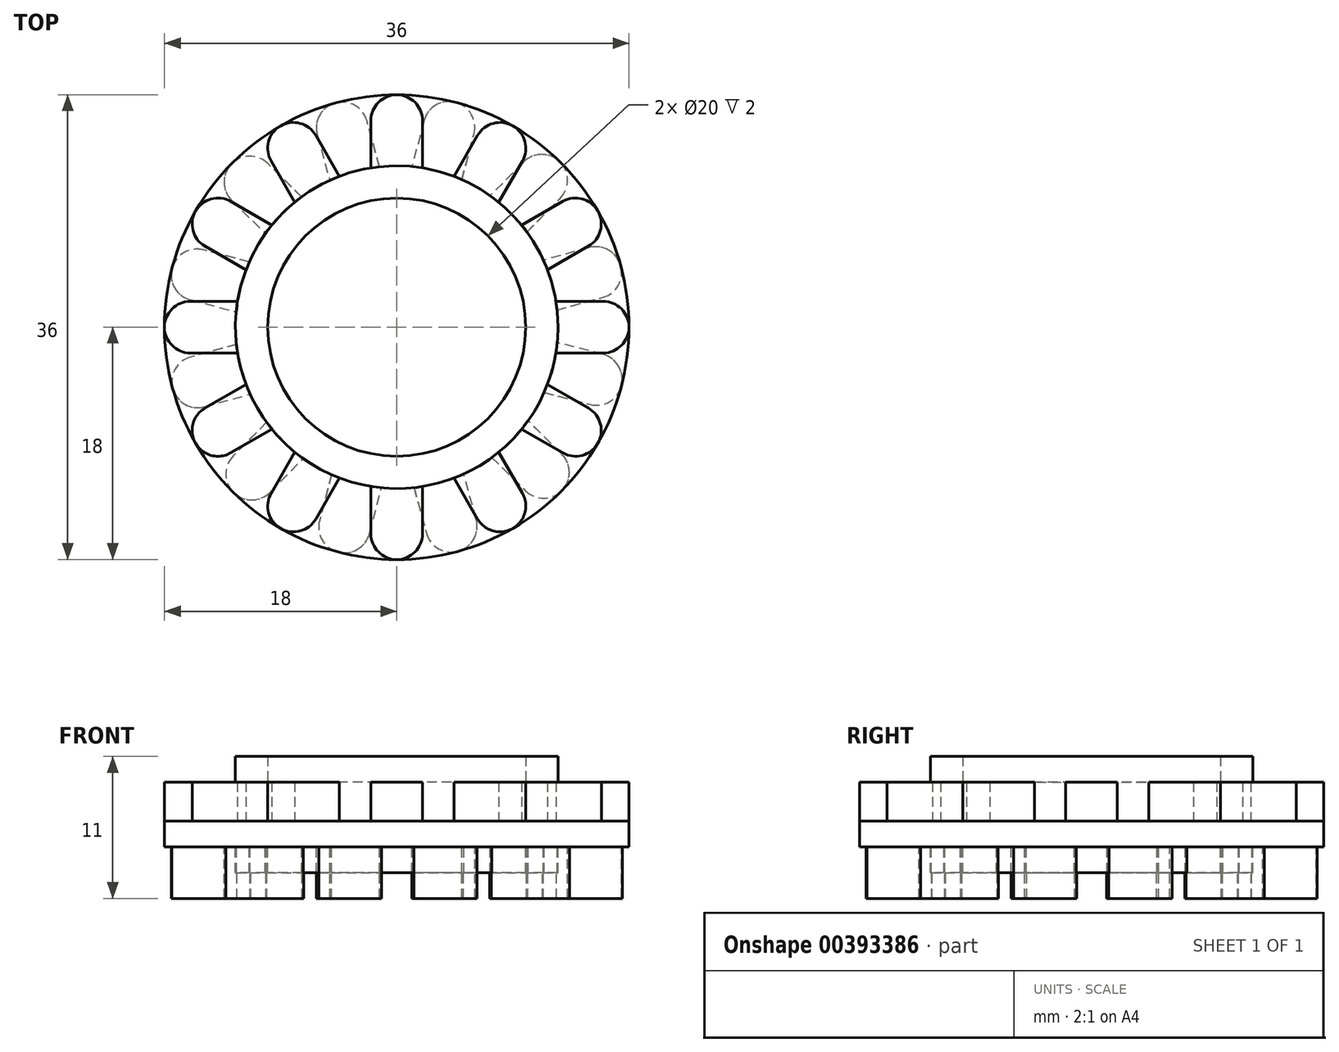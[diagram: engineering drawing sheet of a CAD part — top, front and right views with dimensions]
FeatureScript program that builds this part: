
annotation { "Feature Type Name" : "Feature", "Feature Type Description" : "" }
export const myFeature = defineFeature(function(context is Context, id is Id, definition is map)
    precondition{}
    {
        {
            var Q0;
            Q0=qCreatedBy(makeId("Top.planeOp"),FACE);
            var sketch = newSketch(context, id + "F0", { "sketchPlane" : qUnion([Q0])});
            skCircle(sketch, "E0", {"center": v(0, 0) * mm, "radius": 18 * mm});
            skSolve(sketch);
        }
        {
            var Q0;
            Q0=makeQuery(id+"F0.imprint","IMPRINT",FACE,{"disambiguationData":[TD([[makeQuery(id+"F0.imprint","IMPRINT",EDGE,{"derivedFrom":sQuery(id+"F0.wireOp",EDGE,"E0")}),1.0]])]});
            extrude(context, id + "F1", {"entities" : qUnion([Q0]), "depth" : 2 * mm});
        }
        {
            var Q0;
            Q0=makeQuery(id+"F1.opExtrude","CAP_FACE",FACE,{"disambiguationData":[OSD([sQuery(id+"F0.wireOp",EDGE,"E0")])],"isStart":false});
            var sketch = newSketch(context, id + "F2", { "sketchPlane" : qUnion([Q0])});
            skCircle(sketch, "E1", {"center": v(0, 0) * mm, "radius": 10 * mm});
            skCircle(sketch, "E2", {"center": v(0, 0) * mm, "radius": 12.5 * mm});
            skSolve(sketch);
        }
        {
            var Q0;
            Q0=makeQuery(id+"F2.imprint","IMPRINT",FACE,{"disambiguationData":[TD([[makeQuery(id+"F2.imprint","IMPRINT",EDGE,{"derivedFrom":sQuery(id+"F2.wireOp",EDGE,"E1")}),-1.0]])]});
            extrude(context, id + "F3", {"entities" : qUnion([Q0]), "operationType" : NewBodyOperationType.ADD, "depth" : 5 * mm});
        }
        {
            var Q0;
            Q0 = qSketchRegion(id + "F2", true);
            extrude(context, id + "F4", {"entities" : qUnion([Q0]), "operationType" : NewBodyOperationType.ADD, "oppositeDirection" : true, "depth" : 4 * mm});
        }
        {
            var Q0;
            {var subQ0=sQuery(id+"F0.wireOp",EDGE,"E0");Q0=makeQuery(id+"F3.boolean.opBoolean","SPLIT",FACE,{"disambiguationData":[TD([makeQuery(id+"F1.opExtrude","SWEPT_FACE",FACE,{"disambiguationData":[OSD([subQ0])]})])],"derivedFrom":makeQuery(id+"F1.opExtrude","CAP_FACE",FACE,{"disambiguationData":[OSD([subQ0])],"isStart":false})});}
            var sketch = newSketch(context, id + "F5", { "sketchPlane" : qUnion([Q0])});
            skLineSegment(sketch, "E3.3.0", {"start": v(2, 12.34) * mm, "end": v(2, 16) * mm});
            skLineSegment(sketch, "E3.3.1", {"start": v(-2, 12.34) * mm, "end": v(-2, 16) * mm});
            skPoint(sketch, "E3.center", {"position": v(0, 0) * mm});
            skArc(sketch, "E4", {"start": v(2, 16) * mm, "mid": v(0, 18) * mm, "end": v(-2, 16) * mm});
            skLineSegment(sketch, "E5.1.0", {"start": v(-4.44, 11.69) * mm, "end": v(-6.27, 14.86) * mm});
            skLineSegment(sketch, "E5.1.1", {"start": v(-7.9, 9.69) * mm, "end": v(-9.73, 12.86) * mm});
            skArc(sketch, "E5.1.2", {"start": v(-6.27, 14.86) * mm, "mid": v(-9, 15.59) * mm, "end": v(-9.73, 12.86) * mm});
            skLineSegment(sketch, "E5.2.0", {"start": v(-9.69, 7.9) * mm, "end": v(-12.86, 9.73) * mm});
            skLineSegment(sketch, "E5.2.1", {"start": v(-11.69, 4.44) * mm, "end": v(-14.86, 6.27) * mm});
            skArc(sketch, "E5.2.2", {"start": v(-12.86, 9.73) * mm, "mid": v(-15.59, 9) * mm, "end": v(-14.86, 6.27) * mm});
            skLineSegment(sketch, "E5.3.0", {"start": v(-12.34, 2) * mm, "end": v(-16, 2) * mm});
            skLineSegment(sketch, "E5.3.1", {"start": v(-12.34, -2) * mm, "end": v(-16, -2) * mm});
            skArc(sketch, "E5.3.2", {"start": v(-16, 2) * mm, "mid": v(-18, 0) * mm, "end": v(-16, -2) * mm});
            skLineSegment(sketch, "E5.4.0", {"start": v(-11.69, -4.44) * mm, "end": v(-14.86, -6.27) * mm});
            skLineSegment(sketch, "E5.4.1", {"start": v(-9.69, -7.9) * mm, "end": v(-12.86, -9.73) * mm});
            skArc(sketch, "E5.4.2", {"start": v(-14.86, -6.27) * mm, "mid": v(-15.59, -9) * mm, "end": v(-12.86, -9.73) * mm});
            skLineSegment(sketch, "E5.5.0", {"start": v(-7.9, -9.69) * mm, "end": v(-9.73, -12.86) * mm});
            skLineSegment(sketch, "E5.5.1", {"start": v(-4.44, -11.69) * mm, "end": v(-6.27, -14.86) * mm});
            skArc(sketch, "E5.5.2", {"start": v(-9.73, -12.86) * mm, "mid": v(-9, -15.59) * mm, "end": v(-6.27, -14.86) * mm});
            skLineSegment(sketch, "E5.6.0", {"start": v(-2, -12.34) * mm, "end": v(-2, -16) * mm});
            skLineSegment(sketch, "E5.6.1", {"start": v(2, -12.34) * mm, "end": v(2, -16) * mm});
            skArc(sketch, "E5.6.2", {"start": v(-2, -16) * mm, "mid": v(0, -18) * mm, "end": v(2, -16) * mm});
            skLineSegment(sketch, "E5.7.0", {"start": v(4.44, -11.69) * mm, "end": v(6.27, -14.86) * mm});
            skLineSegment(sketch, "E5.7.1", {"start": v(7.9, -9.69) * mm, "end": v(9.73, -12.86) * mm});
            skArc(sketch, "E5.7.2", {"start": v(6.27, -14.86) * mm, "mid": v(9, -15.59) * mm, "end": v(9.73, -12.86) * mm});
            skLineSegment(sketch, "E5.8.0", {"start": v(9.69, -7.9) * mm, "end": v(12.86, -9.73) * mm});
            skLineSegment(sketch, "E5.8.1", {"start": v(11.69, -4.44) * mm, "end": v(14.86, -6.27) * mm});
            skArc(sketch, "E5.8.2", {"start": v(12.86, -9.73) * mm, "mid": v(15.59, -9) * mm, "end": v(14.86, -6.27) * mm});
            skLineSegment(sketch, "E5.9.0", {"start": v(12.34, -2) * mm, "end": v(16, -2) * mm});
            skLineSegment(sketch, "E5.9.1", {"start": v(12.34, 2) * mm, "end": v(16, 2) * mm});
            skArc(sketch, "E5.9.2", {"start": v(16, -2) * mm, "mid": v(18, 0) * mm, "end": v(16, 2) * mm});
            skLineSegment(sketch, "E5.10.0", {"start": v(11.69, 4.44) * mm, "end": v(14.86, 6.27) * mm});
            skLineSegment(sketch, "E5.10.1", {"start": v(9.69, 7.9) * mm, "end": v(12.86, 9.73) * mm});
            skArc(sketch, "E5.10.2", {"start": v(14.86, 6.27) * mm, "mid": v(15.59, 9) * mm, "end": v(12.86, 9.73) * mm});
            skLineSegment(sketch, "E5.11.0", {"start": v(7.9, 9.69) * mm, "end": v(9.73, 12.86) * mm});
            skLineSegment(sketch, "E5.11.1", {"start": v(4.44, 11.69) * mm, "end": v(6.27, 14.86) * mm});
            skArc(sketch, "E5.11.2", {"start": v(9.73, 12.86) * mm, "mid": v(9, 15.59) * mm, "end": v(6.27, 14.86) * mm});
            skCircle(sketch, "E6", {"center": v(0, 0) * mm, "radius": 12.5 * mm});
            skSolve(sketch);
        }
        {
            var Q0;
            Q0 = qSketchRegion(id + "F5", true);
            extrude(context, id + "F6", {"entities" : qUnion([Q0]), "operationType" : NewBodyOperationType.ADD, "depth" : 3 * mm});
        }
        {
            var Q0;
            {var subQ1=sQuery(id+"F0.wireOp",EDGE,"E0");var subQ2=makeQuery(id+"F1.opExtrude","CAP_FACE",FACE,{"disambiguationData":[OSD([subQ1])],"isStart":false});var subQ3=makeQuery(id+"F1.opExtrude","SWEPT_FACE",FACE,{"disambiguationData":[OSD([subQ1])]});Q0=makeQuery(id+"F6.boolean.opBoolean","SPLIT",FACE,{"disambiguationData":[TD([makeQuery(id+"F6.opExtrude","SWEPT_FACE",FACE,{"disambiguationData":[OSD([sQuery(id+"F5.wireOp",EDGE,"E5.8.1")])]})])],"derivedFrom":makeQuery(id+"F3.boolean.opBoolean","SPLIT",FACE,{"disambiguationData":[TD([subQ3])],"derivedFrom":subQ2})});}
            var sketch = newSketch(context, id + "F7", { "sketchPlane" : qUnion([Q0])});
            skPoint(sketch, "E7.startSnap0", {"position": v(17.41, -1.41) * mm});
            skArc(sketch, "E8", {"start": v(14.97, -5.98) * mm, "mid": v(17.41, -4.55) * mm, "end": v(15.99, -2.11) * mm});
            skLineSegment(sketch, "E9", {"start": v(15.99, -2.11) * mm, "end": v(12.4, -1.17) * mm});
            skLineSegment(sketch, "E10", {"start": v(11.38, -5.04) * mm, "end": v(14.97, -5.98) * mm});
            skPoint(sketch, "E11.orphan", {"position": v(17.41, -4.55) * mm});
            skPoint(sketch, "E7.end.orphan", {"position": v(0, 0) * mm});
            skArc(sketch, "E12", {"start": v(11.38, -5.04) * mm, "mid": v(12.04, -3.15) * mm, "end": v(12.4, -1.17) * mm});
            skLineSegment(sketch, "E13.1.0", {"start": v(14.9, 6.16) * mm, "end": v(11.32, 5.18) * mm});
            skArc(sketch, "E13.1.1", {"start": v(15.96, 2.3) * mm, "mid": v(17.36, 4.76) * mm, "end": v(14.9, 6.16) * mm});
            skLineSegment(sketch, "E13.1.2", {"start": v(12.38, 1.32) * mm, "end": v(15.96, 2.3) * mm});
            skArc(sketch, "E13.1.3", {"start": v(12.38, 1.32) * mm, "mid": v(12, 3.3) * mm, "end": v(11.32, 5.18) * mm});
            skLineSegment(sketch, "E13.2.0", {"start": v(9.82, 12.79) * mm, "end": v(7.21, 10.14) * mm});
            skArc(sketch, "E13.2.1", {"start": v(12.67, 9.98) * mm, "mid": v(12.65, 12.8) * mm, "end": v(9.82, 12.79) * mm});
            skLineSegment(sketch, "E13.2.2", {"start": v(10.06, 7.33) * mm, "end": v(12.67, 9.98) * mm});
            skArc(sketch, "E13.2.3", {"start": v(10.06, 7.33) * mm, "mid": v(8.75, 8.85) * mm, "end": v(7.21, 10.14) * mm});
            skLineSegment(sketch, "E13.3.0", {"start": v(2.11, 15.99) * mm, "end": v(1.17, 12.4) * mm});
            skArc(sketch, "E13.3.1", {"start": v(5.98, 14.97) * mm, "mid": v(4.55, 17.41) * mm, "end": v(2.11, 15.99) * mm});
            skLineSegment(sketch, "E13.3.2", {"start": v(5.04, 11.38) * mm, "end": v(5.98, 14.97) * mm});
            skArc(sketch, "E13.3.3", {"start": v(5.04, 11.38) * mm, "mid": v(3.15, 12.04) * mm, "end": v(1.17, 12.4) * mm});
            skLineSegment(sketch, "E13.4.0", {"start": v(-6.16, 14.9) * mm, "end": v(-5.18, 11.32) * mm});
            skArc(sketch, "E13.4.1", {"start": v(-2.3, 15.96) * mm, "mid": v(-4.76, 17.36) * mm, "end": v(-6.16, 14.9) * mm});
            skLineSegment(sketch, "E13.4.2", {"start": v(-1.32, 12.38) * mm, "end": v(-2.3, 15.96) * mm});
            skArc(sketch, "E13.4.3", {"start": v(-1.32, 12.38) * mm, "mid": v(-3.3, 12) * mm, "end": v(-5.18, 11.32) * mm});
            skLineSegment(sketch, "E13.5.0", {"start": v(-12.79, 9.82) * mm, "end": v(-10.14, 7.21) * mm});
            skArc(sketch, "E13.5.1", {"start": v(-9.98, 12.67) * mm, "mid": v(-12.8, 12.65) * mm, "end": v(-12.79, 9.82) * mm});
            skLineSegment(sketch, "E13.5.2", {"start": v(-7.33, 10.06) * mm, "end": v(-9.98, 12.67) * mm});
            skArc(sketch, "E13.5.3", {"start": v(-7.33, 10.06) * mm, "mid": v(-8.85, 8.75) * mm, "end": v(-10.14, 7.21) * mm});
            skLineSegment(sketch, "E13.6.0", {"start": v(-15.99, 2.11) * mm, "end": v(-12.4, 1.17) * mm});
            skArc(sketch, "E13.6.1", {"start": v(-14.97, 5.98) * mm, "mid": v(-17.41, 4.55) * mm, "end": v(-15.99, 2.11) * mm});
            skLineSegment(sketch, "E13.6.2", {"start": v(-11.38, 5.04) * mm, "end": v(-14.97, 5.98) * mm});
            skArc(sketch, "E13.6.3", {"start": v(-11.38, 5.04) * mm, "mid": v(-12.04, 3.15) * mm, "end": v(-12.4, 1.17) * mm});
            skLineSegment(sketch, "E13.7.0", {"start": v(-14.9, -6.16) * mm, "end": v(-11.32, -5.18) * mm});
            skArc(sketch, "E13.7.1", {"start": v(-15.96, -2.3) * mm, "mid": v(-17.36, -4.76) * mm, "end": v(-14.9, -6.16) * mm});
            skLineSegment(sketch, "E13.7.2", {"start": v(-12.38, -1.32) * mm, "end": v(-15.96, -2.3) * mm});
            skArc(sketch, "E13.7.3", {"start": v(-12.38, -1.32) * mm, "mid": v(-12, -3.3) * mm, "end": v(-11.32, -5.18) * mm});
            skLineSegment(sketch, "E13.8.0", {"start": v(-9.82, -12.79) * mm, "end": v(-7.21, -10.14) * mm});
            skArc(sketch, "E13.8.1", {"start": v(-12.67, -9.98) * mm, "mid": v(-12.65, -12.8) * mm, "end": v(-9.82, -12.79) * mm});
            skLineSegment(sketch, "E13.8.2", {"start": v(-10.06, -7.33) * mm, "end": v(-12.67, -9.98) * mm});
            skArc(sketch, "E13.8.3", {"start": v(-10.06, -7.33) * mm, "mid": v(-8.75, -8.85) * mm, "end": v(-7.21, -10.14) * mm});
            skLineSegment(sketch, "E13.9.0", {"start": v(-2.11, -15.99) * mm, "end": v(-1.17, -12.4) * mm});
            skArc(sketch, "E13.9.1", {"start": v(-5.98, -14.97) * mm, "mid": v(-4.55, -17.41) * mm, "end": v(-2.11, -15.99) * mm});
            skLineSegment(sketch, "E13.9.2", {"start": v(-5.04, -11.38) * mm, "end": v(-5.98, -14.97) * mm});
            skArc(sketch, "E13.9.3", {"start": v(-5.04, -11.38) * mm, "mid": v(-3.15, -12.04) * mm, "end": v(-1.17, -12.4) * mm});
            skLineSegment(sketch, "E13.10.0", {"start": v(6.16, -14.9) * mm, "end": v(5.18, -11.32) * mm});
            skArc(sketch, "E13.10.1", {"start": v(2.3, -15.96) * mm, "mid": v(4.76, -17.36) * mm, "end": v(6.16, -14.9) * mm});
            skLineSegment(sketch, "E13.10.2", {"start": v(1.32, -12.38) * mm, "end": v(2.3, -15.96) * mm});
            skArc(sketch, "E13.10.3", {"start": v(1.32, -12.38) * mm, "mid": v(3.3, -12) * mm, "end": v(5.18, -11.32) * mm});
            skLineSegment(sketch, "E13.11.0", {"start": v(12.79, -9.82) * mm, "end": v(10.14, -7.21) * mm});
            skArc(sketch, "E13.11.1", {"start": v(9.98, -12.67) * mm, "mid": v(12.8, -12.65) * mm, "end": v(12.79, -9.82) * mm});
            skLineSegment(sketch, "E13.11.2", {"start": v(7.33, -10.06) * mm, "end": v(9.98, -12.67) * mm});
            skArc(sketch, "E13.11.3", {"start": v(7.33, -10.06) * mm, "mid": v(8.85, -8.75) * mm, "end": v(10.14, -7.21) * mm});
            skSolve(sketch);
        }
        {
            var Q0;
            Q0 = qSketchRegion(id + "F7", true);
            extrude(context, id + "F8", {"entities" : qUnion([Q0]), "operationType" : NewBodyOperationType.ADD, "oppositeDirection" : true, "depth" : 6 * mm});
        }
    });
